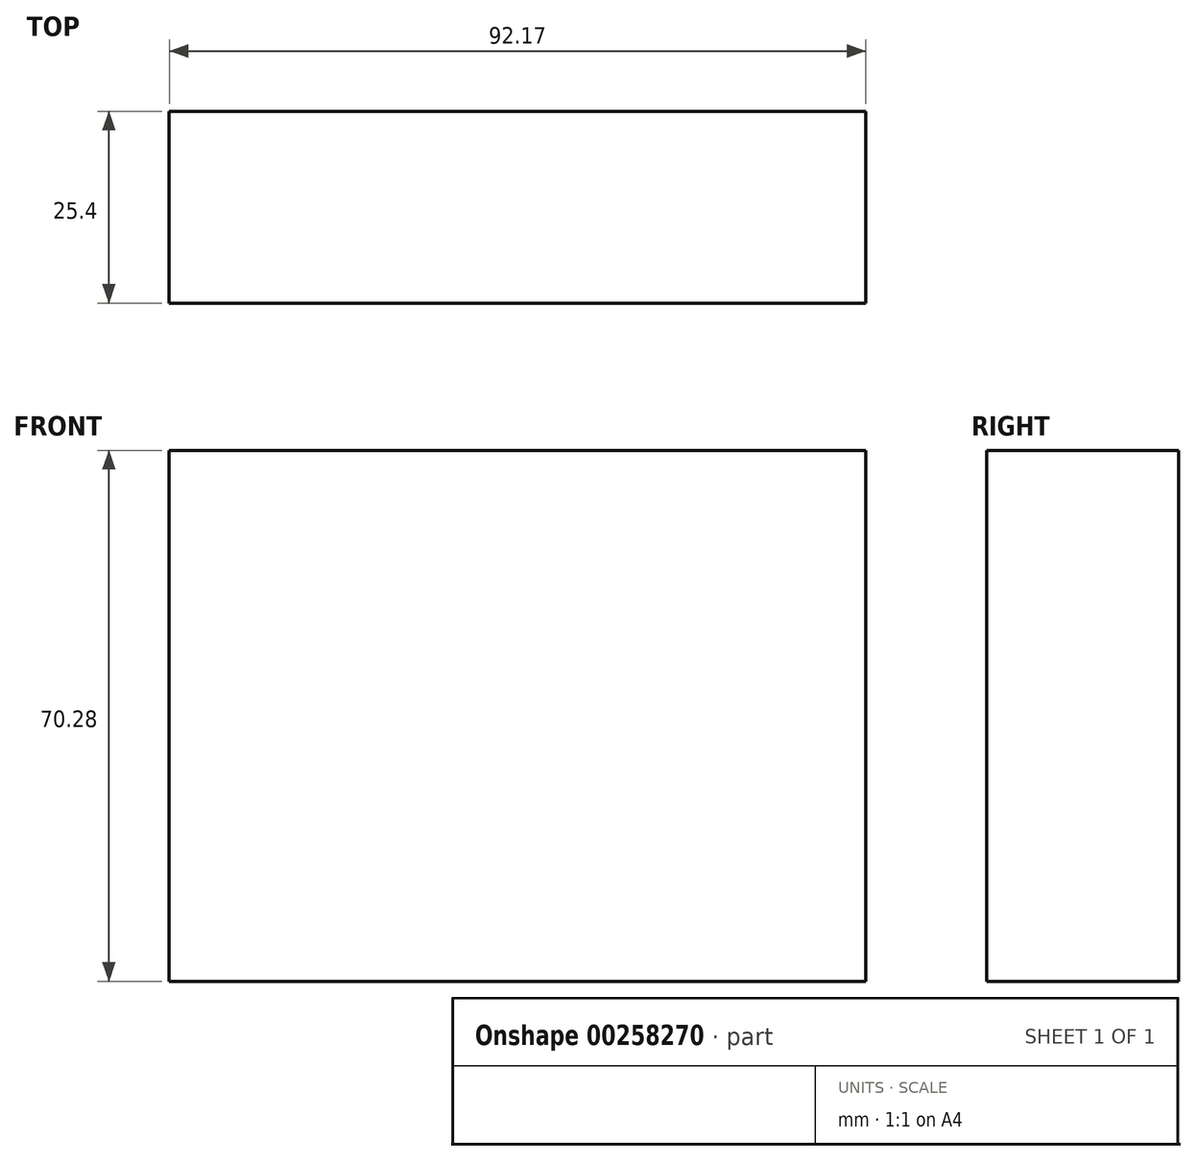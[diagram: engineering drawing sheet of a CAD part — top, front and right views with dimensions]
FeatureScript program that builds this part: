
annotation { "Feature Type Name" : "Feature", "Feature Type Description" : "" }
export const myFeature = defineFeature(function(context is Context, id is Id, definition is map)
    precondition{}
    {
        {
            var Q0;
            Q0=qCreatedBy(makeId("Front.planeOp"),FACE);
            var sketch = newSketch(context, id + "F0", { "sketchPlane" : qUnion([Q0])});
            skLineSegment(sketch, "E0.bottom", {"start": v(-32.21, 31.51) * mm, "end": v(34.56, 31.51) * mm});
            skLineSegment(sketch, "E0.top", {"start": v(-32.21, -38.77) * mm, "end": v(34.56, -38.77) * mm});
            skLineSegment(sketch, "E0.left", {"start": v(-32.21, 31.51) * mm, "end": v(-32.21, -38.77) * mm});
            skLineSegment(sketch, "E0.right", {"start": v(34.56, 31.51) * mm, "end": v(34.56, -38.77) * mm});
            skSolve(sketch);
        }
        {
            var Q0;
            Q0=makeQuery(id+"F0.imprint","IMPRINT",FACE,{"disambiguationData":[TD([[makeQuery(id+"F0.imprint","IMPRINT",EDGE,{"derivedFrom":sQuery(id+"F0.wireOp",EDGE,"E0.bottom")}),-1.0]])]});
            extrude(context, id + "F1", {"entities" : qUnion([Q0]), "depth" : 25.4 * mm});
        }
        {
            var Q0;
            Q0=makeQuery(id+"F1.opExtrude","SWEPT_FACE",FACE,{"disambiguationData":[OSD([sQuery(id+"F0.wireOp",EDGE,"E0.left")])]});
            var sketch = newSketch(context, id + "F2", { "sketchPlane" : qUnion([Q0])});
            skSolve(sketch);
        }
        {
            var Q0;
            {var subQ0=sQuery(id+"F0.wireOp",EDGE,"E0.left");Q0=makeQuery(id+"F2.imprint","IMPRINT",FACE,{"disambiguationData":[TD([[makeQuery(id+"F2.imprint","IMPRINT",EDGE,{"derivedFrom":makeQuery(id+"F1.opExtrude","CAP_EDGE",EDGE,{"disambiguationData":[OSD([subQ0])],"isStart":true})}),1.0]])]});}
            extrude(context, id + "F3", {"entities" : qUnion([Q0]), "operationType" : NewBodyOperationType.ADD, "depth" : 25.4 * mm});
        }
    });
